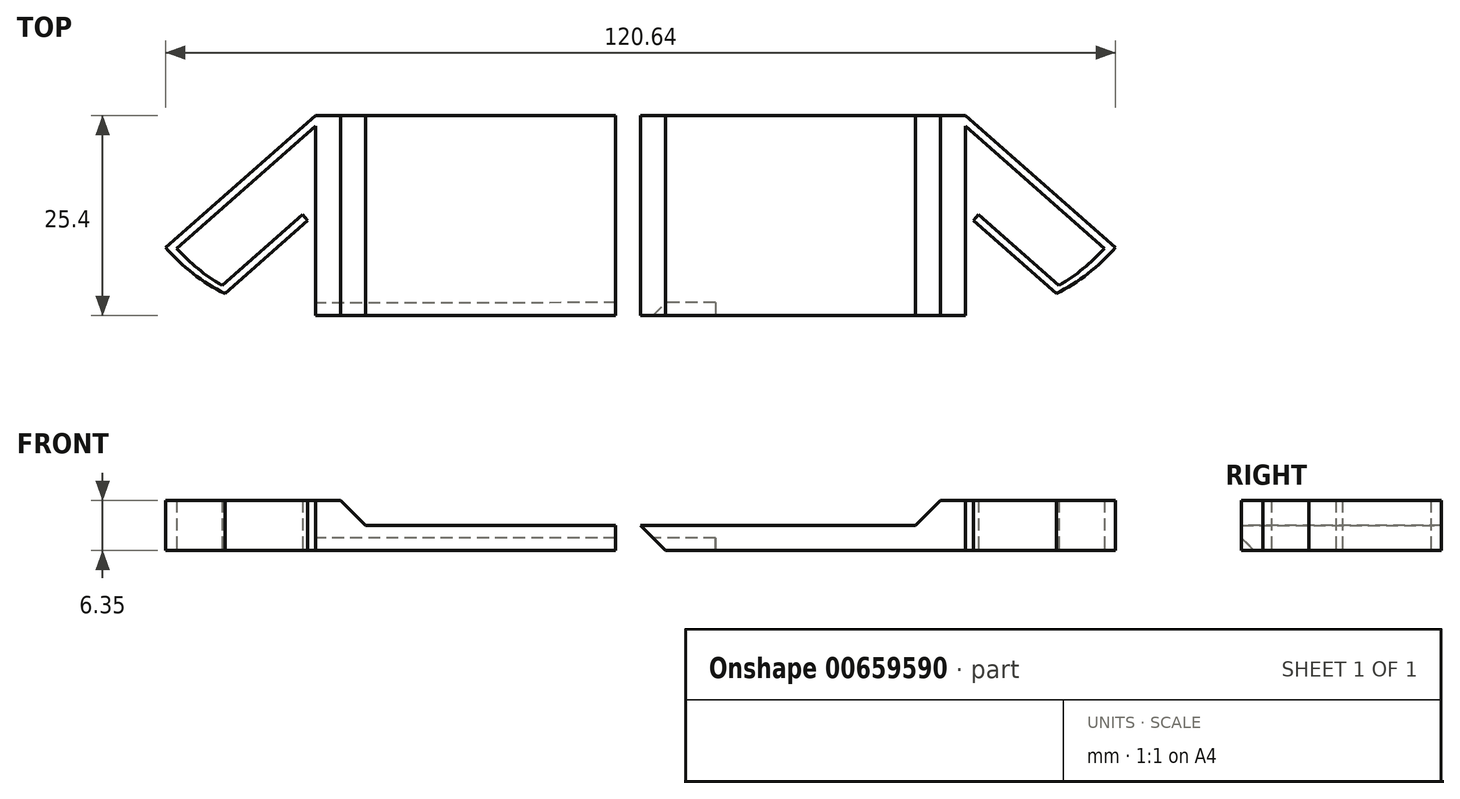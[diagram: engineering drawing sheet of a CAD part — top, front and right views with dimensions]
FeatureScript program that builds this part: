
annotation { "Feature Type Name" : "Feature", "Feature Type Description" : "" }
export const myFeature = defineFeature(function(context is Context, id is Id, definition is map)
    precondition{}
    {
        {
            var Q0;
            Q0=qCreatedBy(makeId("Top.planeOp"),FACE);
            var sketch = newSketch(context, id + "F0", { "sketchPlane" : qUnion([Q0])});
            skLineSegment(sketch, "E0.bottom", {"start": v(28.58, -12.7) * mm, "end": v(-28.58, -12.7) * mm});
            skLineSegment(sketch, "E0.top", {"start": v(28.58, 12.7) * mm, "end": v(-28.58, 12.7) * mm});
            skLineSegment(sketch, "E0.left", {"start": v(28.58, -12.7) * mm, "end": v(28.58, 12.7) * mm});
            skLineSegment(sketch, "E0.right", {"start": v(-28.57, -12.7) * mm, "end": v(-28.57, 12.7) * mm});
            skPoint(sketch, "E0.middle", {"position": v(0, 0) * mm});
            skLineSegment(sketch, "E1", {"start": v(-9.53, 11.37) * mm, "end": v(-9.52, -12.7) * mm});
            skLineSegment(sketch, "E2", {"start": v(0, -12.7) * mm, "end": v(0, 12.7) * mm});
            skPoint(sketch, "E3", {"position": v(-22.22, -12.7) * mm});
            skLineSegment(sketch, "E4", {"start": v(-9.53, 12.7) * mm, "end": v(-28.57, -4.1) * mm});
            skPoint(sketch, "E5", {"position": v(-19.05, -12.7) * mm});
            skArc(sketch, "E6", {"start": v(-28.57, -4.1) * mm, "mid": v(-25.09, -7.37) * mm, "end": v(-21.05, -9.94) * mm});
            skLineSegment(sketch, "E7", {"start": v(-21.05, -9.94) * mm, "end": v(-10.53, -0.66) * mm});
            skLineSegment(sketch, "E8", {"start": v(-10.53, -0.66) * mm, "end": v(-11.19, 0.1) * mm});
            skLineSegment(sketch, "E9", {"start": v(-11.19, 0.1) * mm, "end": v(-11.19, 0.1) * mm});
            skLineSegment(sketch, "E10", {"start": v(-9.53, 11.37) * mm, "end": v(-27.15, -4.18) * mm});
            skArc(sketch, "E11", {"start": v(-27.15, -4.18) * mm, "mid": v(-24.46, -6.77) * mm, "end": v(-21.4, -8.91) * mm});
            skLineSegment(sketch, "E12", {"start": v(-21.4, -8.91) * mm, "end": v(-11.19, 0.1) * mm});
            skSolve(sketch);
        }
        {
            var Q0;
            {var subQ0=sQuery(id+"F0.wireOp",EDGE,"E0.left");Q0=makeQuery(id+"F0.imprint","IMPRINT",FACE,{"disambiguationData":[TD([[makeQuery(id+"F0.imprint","IMPRINT",EDGE,{"derivedFrom":subQ0}),1.0]])]});}
            var Q1;
            {var subQ1=sQuery(id+"F0.wireOp",EDGE,"E1");Q1=makeQuery(id+"F0.imprint","IMPRINT",FACE,{"disambiguationData":[TD([[makeQuery(id+"F0.imprint","IMPRINT",EDGE,{"derivedFrom":subQ1}),1.0]])]});}
            var Q2;
            {var subQ0=sQuery(id+"F0.wireOp",EDGE,"Ll8NUgnO-918t-zldm-zNWz-RsUZQomu35K8");Q2=makeQuery(id+"F0.imprint","IMPRINT",FACE,{"disambiguationData":[TD([[makeQuery(id+"F0.imprint","IMPRINT",EDGE,{"derivedFrom":subQ0}),1.0]])]});}
            extrude(context, id + "F1", {"entities" : qUnion([Q0, Q1, Q2]), "depth" : 3.17 * mm, "offsetDistance" : 25.4 * mm});
        }
        {
            var Q0;
            {var subQ1=sQuery(id+"F0.wireOp",EDGE,"E1");Q0=makeQuery(id+"F0.imprint","IMPRINT",FACE,{"disambiguationData":[TD([[makeQuery(id+"F0.imprint","IMPRINT",EDGE,{"derivedFrom":subQ1}),1.0]])]});}
            extrude(context, id + "F2", {"entities" : qUnion([Q0]), "operationType" : NewBodyOperationType.ADD, "depth" : 6.35 * mm, "offsetDistance" : 25.4 * mm});
        }
        {
            var Q0;
            Q0=makeQuery(id+"F2.opExtrude","CAP_EDGE",EDGE,{"disambiguationData":[OSD([sQuery(id+"F0.wireOp",EDGE,"E2")])],"isStart":false});
            chamfer(context, id + "F3", {"entities" : qUnion([Q0]), "width" : 6.35 * mm, "tangentPropagation" : true});
        }
        {
            var Q0;
            {var subQ0=sQuery(id+"F0.wireOp",EDGE,"E0.left");Q0=makeQuery(id+"F37SAEC6IVc2ddh_1.boolean.opBoolean","MERGE",FACE,{"derivedFrom":[makeQuery(id+"F1.opExtrude","SWEPT_FACE",FACE,{"disambiguationData":[OSD([subQ0])]}),makeQuery(id+"F37SAEC6IVc2ddh_1.opExtrude","SWEPT_FACE",FACE,{"disambiguationData":[OSD([subQ0])]})]});}
            cPlane(context, id + "F4", {"entities" : qUnion([Q0]), "cplaneType" : CPlaneType.OFFSET, "offset" : 3.17 * mm, "width" : 152.4 * mm, "height" : 152.4 * mm});
        }
        {
            var Q0;
            Q0=makeQuery(id+"F1.opExtrude","SWEPT_BODY",BODY,{"disambiguationData":[OSD([sQuery(id+"F0.wireOp",EDGE,"E0.bottom"),sQuery(id+"F0.wireOp",EDGE,"E0.top"),sQuery(id+"F0.wireOp",EDGE,"E0.left"),sQuery(id+"F0.wireOp",EDGE,"E1"),sQuery(id+"F0.wireOp",EDGE,"E4"),sQuery(id+"F0.wireOp",EDGE,"E6"),sQuery(id+"F0.wireOp",EDGE,"E7"),sQuery(id+"F0.wireOp",EDGE,"E8"),sQuery(id+"F0.wireOp",EDGE,"E10"),sQuery(id+"F0.wireOp",EDGE,"E11"),sQuery(id+"F0.wireOp",EDGE,"E12")])]});
            var Q1;
            Q1=qCreatedBy(id+"F4.planeOp",FACE);
            mirror(context, id + "F5", {"entities" : qUnion([Q0]), "mirrorPlane" : qUnion([Q1])});
        }
        {
            var Q0;
            {var subQ0=sQuery(id+"F0.wireOp",EDGE,"E0.bottom");Q0=makeQuery(id+"F2.boolean.opBoolean","MERGE",FACE,{"derivedFrom":[makeQuery(id+"F1.opExtrude","SWEPT_FACE",FACE,{"disambiguationData":[OSD([subQ0])]}),makeQuery(id+"F2.opExtrude","SWEPT_FACE",FACE,{"disambiguationData":[OSD([subQ0])]})]});}
            var sketch = newSketch(context, id + "F6", { "sketchPlane" : qUnion([Q0])});
            skLineSegment(sketch, "E13", {"start": v(28.57, 3.18) * mm, "end": v(31.75, 3.18) * mm});
            skLineSegment(sketch, "E14", {"start": v(31.75, 3.17) * mm, "end": v(28.57, 0) * mm});
            skLineSegment(sketch, "E15", {"start": v(28.57, 0) * mm, "end": v(28.57, 3.18) * mm});
            skLineSegment(sketch, "E16", {"start": v(31.75, 3.18) * mm, "end": v(34.92, 3.18) * mm});
            skLineSegment(sketch, "E17", {"start": v(34.92, 0) * mm, "end": v(31.75, 3.18) * mm});
            skLineSegment(sketch, "E18", {"start": v(34.92, 0) * mm, "end": v(34.92, 3.18) * mm});
            skSolve(sketch);
        }
        {
            var Q0;
            Q0=makeQuery(id+"F6.imprint","IMPRINT",FACE,{"disambiguationData":[TD([[makeQuery(id+"F6.imprint","IMPRINT",EDGE,{"derivedFrom":sQuery(id+"F6.wireOp",EDGE,"E16")}),-1.0]])]});
            var Q1;
            Q1=makeQuery(id+"F6.imprint","IMPRINT",FACE,{"disambiguationData":[TD([[makeQuery(id+"F6.imprint","IMPRINT",EDGE,{"derivedFrom":sQuery(id+"F6.wireOp",EDGE,"E13")}),-1.0]])]});
            var Q2;
            {var subQ0=sQuery(id+"F0.wireOp",EDGE,"E0.bottom");Q2=makeQuery(id+"F5.opPattern","COPY",FACE,{"derivedFrom":makeQuery(id+"F2.boolean.opBoolean","MERGE",FACE,{"derivedFrom":[makeQuery(id+"F1.opExtrude","SWEPT_FACE",FACE,{"disambiguationData":[OSD([subQ0])]}),makeQuery(id+"F2.opExtrude","SWEPT_FACE",FACE,{"disambiguationData":[OSD([subQ0])]})]}),"instanceName":"1"});}
            var Q3;
            Q3=makeQuery(id+"F6.imprint","IMPRINT",FACE,{"disambiguationData":[TD([[makeQuery(id+"F6.imprint","IMPRINT",EDGE,{"derivedFrom":sQuery(id+"F6.wireOp",EDGE,"E15")}),-1.0]])]});
            extrude(context, id + "F7", {"entities" : qUnion([Q0, Q1, Q2, Q3]), "operationType" : NewBodyOperationType.ADD, "oppositeDirection" : true, "depth" : 25.4 * mm, "offsetDistance" : 25.4 * mm});
        }
        {
            var Q0;
            {var subQ0=sQuery(id+"F0.wireOp",EDGE,"E0.bottom");Q0=makeQuery(id+"F7.boolean.opBoolean","MERGE",FACE,{"derivedFrom":[makeQuery(id+"F5.opPattern","COPY",FACE,{"derivedFrom":makeQuery(id+"F2.boolean.opBoolean","MERGE",FACE,{"derivedFrom":[makeQuery(id+"F1.opExtrude","SWEPT_FACE",FACE,{"disambiguationData":[OSD([subQ0])]}),makeQuery(id+"F2.opExtrude","SWEPT_FACE",FACE,{"disambiguationData":[OSD([subQ0])]})]}),"instanceName":"1"}),makeQuery(id+"F7.opExtrude","CAP_FACE",FACE,{"disambiguationData":[OSD([subQ0])],"isStart":true}),makeQuery(id+"F7.opExtrude","CAP_FACE",FACE,{"disambiguationData":[OSD([sQuery(id+"F6.wireOp",EDGE,"E16"),sQuery(id+"F6.wireOp",EDGE,"E17"),sQuery(id+"F6.wireOp",EDGE,"E18")])],"isStart":true})]});}
            extrude(context, id + "F8", {"entities" : qUnion([Q0]), "operationType" : NewBodyOperationType.ADD, "depth" : 25.4 * mm, "offsetDistance" : 25.4 * mm});
        }
        {
            var Q0;
            {var subQ0=sQuery(id+"F0.wireOp",EDGE,"E1");Q0=makeQuery(id+"F8.boolean.opBoolean","MERGE",FACE,{"derivedFrom":[makeQuery(id+"F5.opPattern","COPY",FACE,{"derivedFrom":makeQuery(id+"F2.boolean.opBoolean","MERGE",FACE,{"derivedFrom":[makeQuery(id+"F1.opExtrude","SWEPT_FACE",FACE,{"disambiguationData":[OSD([subQ0])]}),makeQuery(id+"F2.opExtrude","SWEPT_FACE",FACE,{"disambiguationData":[OSD([subQ0])]})]}),"instanceName":"1"}),makeQuery(id+"F8.opExtrude","SWEPT_FACE",FACE,{"disambiguationData":[OSD([sQuery(id+"F0.wireOp",EDGE,"E0.bottom"),subQ0])]})]});}
            var sketch = newSketch(context, id + "F9", { "sketchPlane" : qUnion([Q0])});
            skPoint(sketch, "E19.oppositeSnap0", {"position": v(-12.7, 6.35) * mm});
            skPoint(sketch, "E19.oppositeSnap1", {"position": v(-38.1, 3.18) * mm});
            skLineSegment(sketch, "E19.bottom", {"start": v(-38.1, 6.35) * mm, "end": v(-12.7, 6.35) * mm});
            skLineSegment(sketch, "E19.top", {"start": v(-38.1, 3.18) * mm, "end": v(-12.7, 3.18) * mm});
            skLineSegment(sketch, "E19.left", {"start": v(-38.1, 6.35) * mm, "end": v(-38.1, 3.18) * mm});
            skLineSegment(sketch, "E19.right", {"start": v(-12.7, 6.35) * mm, "end": v(-12.7, 3.18) * mm});
            skSolve(sketch);
        }
        {
            var Q0;
            Q0 = qSketchRegion(id + "F9", true);
            extrude(context, id + "F10", {"entities" : qUnion([Q0]), "operationType" : NewBodyOperationType.REMOVE, "oppositeDirection" : true, "depth" : 25.4 * mm, "offsetDistance" : 25.4 * mm});
        }
        {
            var Q0;
            {var subQ0=sQuery(id+"F0.wireOp",EDGE,"E1");Q0=makeQuery(id+"F8.boolean.opBoolean","MERGE",FACE,{"derivedFrom":[makeQuery(id+"F5.opPattern","COPY",FACE,{"derivedFrom":makeQuery(id+"F2.boolean.opBoolean","MERGE",FACE,{"derivedFrom":[makeQuery(id+"F1.opExtrude","SWEPT_FACE",FACE,{"disambiguationData":[OSD([subQ0])]}),makeQuery(id+"F2.opExtrude","SWEPT_FACE",FACE,{"disambiguationData":[OSD([subQ0])]})]}),"instanceName":"1"}),makeQuery(id+"F8.opExtrude","SWEPT_FACE",FACE,{"disambiguationData":[OSD([sQuery(id+"F0.wireOp",EDGE,"E0.bottom"),subQ0])]})]});}
            var sketch = newSketch(context, id + "F11", { "sketchPlane" : qUnion([Q0])});
            skLineSegment(sketch, "E20", {"start": v(-12.7, 0) * mm, "end": v(-12.7, 1.6) * mm});
            skPoint(sketch, "E20.startSnap0", {"position": v(-13.37, 0) * mm});
            skLineSegment(sketch, "E21", {"start": v(-12.7, 1.6) * mm, "end": v(-11.1, 0) * mm});
            skLineSegment(sketch, "E22", {"start": v(-11.1, 0) * mm, "end": v(-12.7, 0) * mm});
            skSolve(sketch);
        }
        {
            var Q0;
            Q0=makeQuery(id+"F11.imprint","IMPRINT",FACE,{"disambiguationData":[TD([[makeQuery(id+"F11.imprint","IMPRINT",EDGE,{"derivedFrom":sQuery(id+"F11.wireOp",EDGE,"E20")}),-1.0]])]});
            extrude(context, id + "F12", {"entities" : qUnion([Q0]), "operationType" : NewBodyOperationType.REMOVE, "endBound" : BoundingType.THROUGH_ALL, "oppositeDirection" : true, "depth" : 50.8 * mm, "offsetDistance" : 25.4 * mm});
        }
        {
            var Q0;
            {var subQ0=sQuery(id+"F0.wireOp",EDGE,"E1");Q0=makeQuery(id+"F2.boolean.opBoolean","MERGE",FACE,{"derivedFrom":[makeQuery(id+"F1.opExtrude","SWEPT_FACE",FACE,{"disambiguationData":[OSD([subQ0])]}),makeQuery(id+"F2.opExtrude","SWEPT_FACE",FACE,{"disambiguationData":[OSD([subQ0])]})]});}
            var sketch = newSketch(context, id + "F13", { "sketchPlane" : qUnion([Q0])});
            skLineSegment(sketch, "E23", {"start": v(12.7, 0) * mm, "end": v(11.1, 0) * mm});
            skLineSegment(sketch, "E24", {"start": v(11.1, 0) * mm, "end": v(12.7, 1.6) * mm});
            skLineSegment(sketch, "E25", {"start": v(12.7, 1.6) * mm, "end": v(12.7, 0) * mm});
            skSolve(sketch);
        }
        {
            var Q0;
            Q0=makeQuery(id+"F13.imprint","IMPRINT",FACE,{"disambiguationData":[TD([[makeQuery(id+"F13.imprint","IMPRINT",EDGE,{"derivedFrom":sQuery(id+"F13.wireOp",EDGE,"E23")}),1.0]])]});
            extrude(context, id + "F14", {"entities" : qUnion([Q0]), "operationType" : NewBodyOperationType.REMOVE, "oppositeDirection" : true, "depth" : 50.8 * mm, "offsetDistance" : 25.4 * mm});
        }
    });
